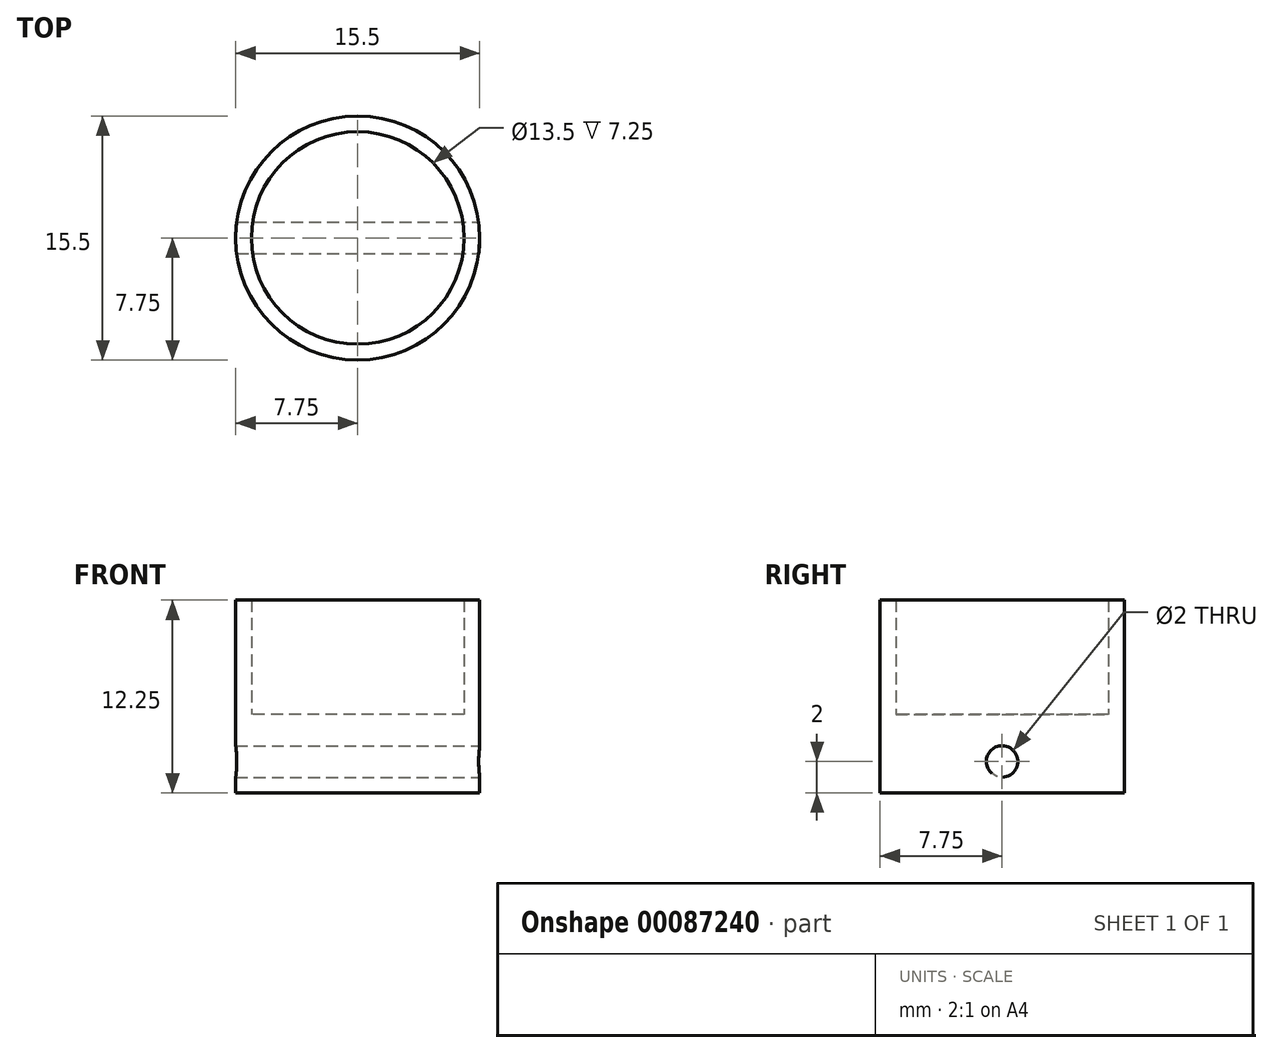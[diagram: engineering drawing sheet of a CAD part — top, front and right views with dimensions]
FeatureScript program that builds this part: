
annotation { "Feature Type Name" : "Feature", "Feature Type Description" : "" }
export const myFeature = defineFeature(function(context is Context, id is Id, definition is map)
    precondition{}
    {
        {
            var Q0;
            Q0=qCreatedBy(makeId("Top.planeOp"),FACE);
            var sketch = newSketch(context, id + "F0", { "sketchPlane" : qUnion([Q0])});
            skCircle(sketch, "E0", {"center": v(0, 0) * mm, "radius": 6.75 * mm});
            skCircle(sketch, "E1.0", {"center": v(0, 0) * mm, "radius": 7.75 * mm});
            skSolve(sketch);
        }
        {
            var Q0;
            Q0 = qSketchRegion(id + "F0", true);
            extrude(context, id + "F1", {"entities" : qUnion([Q0]), "depth" : 7.25 * mm});
        }
        {
            var Q0;
            Q0=makeQuery(id+"F0.imprint","IMPRINT",FACE,{"disambiguationData":[TD([[makeQuery(id+"F0.imprint","IMPRINT",EDGE,{"derivedFrom":sQuery(id+"F0.wireOp",EDGE,"E0")}),1.0]])]});
            var Q1;
            Q1=makeQuery(id+"F0.imprint","IMPRINT",FACE,{"disambiguationData":[TD([[makeQuery(id+"F0.imprint","IMPRINT",EDGE,{"derivedFrom":sQuery(id+"F0.wireOp",EDGE,"E0")}),-1.0]])]});
            extrude(context, id + "F2", {"entities" : qUnion([Q0, Q1]), "operationType" : NewBodyOperationType.ADD, "oppositeDirection" : true, "depth" : 5 * mm});
        }
        {
            var Q0;
            Q0=qCreatedBy(makeId("Right.planeOp"),FACE);
            var sketch = newSketch(context, id + "F3", { "sketchPlane" : qUnion([Q0])});
            skPoint(sketch, "E2.0", {"position": v(0, 0) * mm});
            skPoint(sketch, "E3", {"position": v(0, -3) * mm});
            skSolve(sketch);
        }
        {
            var Q0;
            Q0=sQuery(id+"F3.wireOp",VERTEX,"E3");
            var Q1;
            Q1=makeQuery(id+"F1.opExtrude","SWEPT_BODY",BODY,{"disambiguationData":[OSD([sQuery(id+"F0.wireOp",EDGE,"E0"),sQuery(id+"F0.wireOp",EDGE,"E1.0")])]});
            hole(context, id + "F4", {"style" : HoleStyle.SIMPLE, "endStyle" : HoleEndStyle.THROUGH, "holeDiameter" : 2 * mm, "locations" : qUnion([Q0]), "scope" : qUnion([Q1]), "isTappedThrough" : true});
        }
        {
            var Q0;
            Q0=sQuery(id+"F3.wireOp",VERTEX,"E3");
            var Q1;
            Q1=makeQuery(id+"F1.opExtrude","SWEPT_BODY",BODY,{"disambiguationData":[OSD([sQuery(id+"F0.wireOp",EDGE,"E0"),sQuery(id+"F0.wireOp",EDGE,"E1.0")])]});
            hole(context, id + "F5", {"style" : HoleStyle.SIMPLE, "endStyle" : HoleEndStyle.THROUGH, "oppositeDirection" : true, "holeDiameter" : 2 * mm, "locations" : qUnion([Q0]), "scope" : qUnion([Q1]), "isTappedThrough" : true});
        }
    });
